# Revit family: IVLB_PML_LF_Dura 270mm WM_Plastic
name_source: partatom
category: Lighting Fixtures
units: mm (PartAtom-declared; Revit-internal decimal feet)

## family parameters
Always vertical = Yes
Cut with Voids When Loaded = No
Light Source = Yes
OmniClass Number = 23.80.70.11.11
OmniClass Title = General Luminaries, Non Directional
Part Type = Normal
Room Calculation Point = Yes
Round Connector Dimension = Use Diameter
Shared = No
Work Plane-Based = No

## types (4) — shared parameters
Apparent Load = 9 VA
Assembly Code = 63.0
Color Filter = 16777215
Description = Surface Mounted
Dimming Lamp Color Temperature Shift = <None>
Emit Shape Visible in Rendering = No
Emit from Circle Diameter = 260 mm
IK Value = IK10
IP Value = IP64
IfcExportAs = IfcLightFixtureType
IfcExportType = USERDEFINED
Lamp = LED
Load Classification = Lighting
Luminaire_Body_Material = Select RGB value
Manufacturer = Pragmalux - Distrilight
Model = Dura
Tilt Angle = 90.00°
URL = https://www.pragmalux.com
Voltage = 230 V
Wattage Comments = 9W

## per-type parameters (varying)
| type | Photometric Web File | Type Comments |
| Dura-S Ø270 IP64 IK10 4-9W 375-1000lm 2200K-2700K 2-CCT | Dura-S Ø270 IP64 IK10 4-9W 375-1000lm 2200K-2700K 2-CCT.ies |  |
| Dura-S Ø270 IP64 IK10 4-9W 450-1100lm 3000K-3500K-4000K 3-CCT | Dura-S Ø270 IP64 IK10 4-9W 450-1100lm 3000K-3500K-4000K 3-CCT.ies |  |
| Dura-S Ø270 IP64 IK10 9W 2200K-2700K 2-CCT DALI | Dura-S Ø270 IP64 IK10 9W 2200K-2700K 2-CCT DALI.ies | DALI |
| Dura-S Ø270 IP64 IK10 9W 3000K-3500K-4000K 3-CCT DALI | Dura-S Ø270 IP64 IK10 9W 3000K-3500K-4000K 3-CCT DALI.ies |  |

## geometry (parser evidence)
native form markers: Sweep x6
no freeform markers — native parametric forms only
